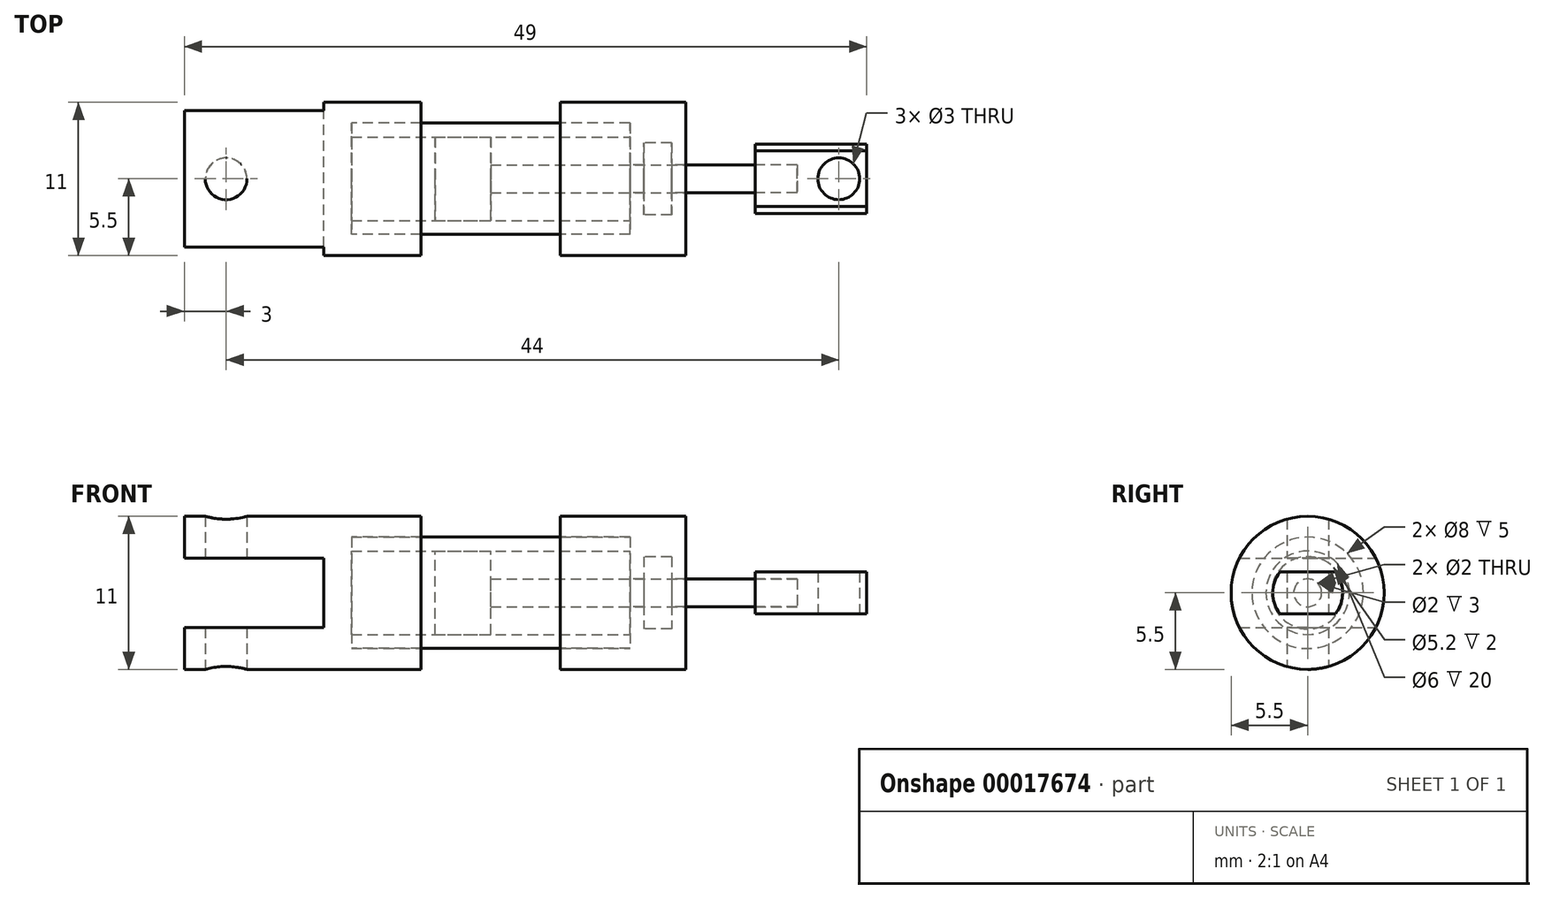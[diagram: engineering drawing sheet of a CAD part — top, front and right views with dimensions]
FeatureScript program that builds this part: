
annotation { "Feature Type Name" : "Feature", "Feature Type Description" : "" }
export const myFeature = defineFeature(function(context is Context, id is Id, definition is map)
    precondition{}
    {
        {
            var Q0;
            Q0=qCreatedBy(makeId("Front.planeOp"),FACE);
            var sketch = newSketch(context, id + "F0", { "sketchPlane" : qUnion([Q0])});
            skLineSegment(sketch, "E0", {"start": v(0, 0) * mm, "end": v(-30.47, 0) * mm, "construction": true});
            skLineSegment(sketch, "E1", {"start": v(0, 0) * mm, "end": v(0, 1) * mm});
            skLineSegment(sketch, "E2", {"start": v(0, 1) * mm, "end": v(-22, 1) * mm});
            skLineSegment(sketch, "E3", {"start": v(-22, 1) * mm, "end": v(-22, 3) * mm});
            skLineSegment(sketch, "E4", {"start": v(-22, 3) * mm, "end": v(-26, 3) * mm});
            skLineSegment(sketch, "E5", {"start": v(-26, 3) * mm, "end": v(-26, 0) * mm});
            skLineSegment(sketch, "E6", {"start": v(-26, 0) * mm, "end": v(0, 0) * mm});
            skLineSegment(sketch, "E7", {"start": v(-12, 3) * mm, "end": v(-12, 4) * mm});
            skLineSegment(sketch, "E8", {"start": v(-12, 4) * mm, "end": v(-32, 4) * mm});
            skLineSegment(sketch, "E9", {"start": v(-32, 4) * mm, "end": v(-32, 3) * mm});
            skLineSegment(sketch, "E10", {"start": v(-27, 3) * mm, "end": v(-12, 3) * mm});
            skLineSegment(sketch, "E11", {"start": v(-17, 4) * mm, "end": v(-17, 5.5) * mm});
            skLineSegment(sketch, "E12", {"start": v(-17, 5.5) * mm, "end": v(-8, 5.5) * mm});
            skLineSegment(sketch, "E13", {"start": v(-8, 5.5) * mm, "end": v(-8, 1) * mm});
            skLineSegment(sketch, "E14", {"start": v(-8, 1) * mm, "end": v(-12, 1) * mm});
            skLineSegment(sketch, "E15", {"start": v(-12, 1) * mm, "end": v(-12, 3) * mm});
            skLineSegment(sketch, "E16.bottom", {"start": v(-11, 1) * mm, "end": v(-9, 1) * mm});
            skLineSegment(sketch, "E16.top", {"start": v(-11, 2.6) * mm, "end": v(-9, 2.6) * mm});
            skLineSegment(sketch, "E16.left", {"start": v(-11, 1) * mm, "end": v(-11, 2.6) * mm});
            skLineSegment(sketch, "E16.right", {"start": v(-9, 1) * mm, "end": v(-9, 2.6) * mm});
            skLineSegment(sketch, "E17", {"start": v(-3, 1) * mm, "end": v(-3, 2.5) * mm});
            skLineSegment(sketch, "E18", {"start": v(-3, 2.5) * mm, "end": v(5, 2.5) * mm});
            skLineSegment(sketch, "E19", {"start": v(5, 2.5) * mm, "end": v(5, 0) * mm});
            skLineSegment(sketch, "E20", {"start": v(5, 0) * mm, "end": v(0, 0) * mm});
            skLineSegment(sketch, "E21", {"start": v(-27, 3) * mm, "end": v(-32, 3) * mm});
            skPoint(sketch, "E22.start.orphan", {"position": v(-32, 0) * mm});
            skLineSegment(sketch, "E23", {"start": v(-27, 4) * mm, "end": v(-27, 5.5) * mm});
            skLineSegment(sketch, "E24", {"start": v(-27, 5.5) * mm, "end": v(-44, 5.5) * mm});
            skLineSegment(sketch, "E25", {"start": v(-44, 5.5) * mm, "end": v(-44, 0) * mm});
            skLineSegment(sketch, "E26", {"start": v(-44, 0) * mm, "end": v(-32, 0) * mm});
            skLineSegment(sketch, "E27", {"start": v(-32, 3) * mm, "end": v(-32, 0) * mm});
            skSolve(sketch);
        }
        {
            var Q0;
            {var subQ7=sQuery(id+"F0.wireOp",EDGE,"E7");Q0=makeQuery(id+"F0.imprint","IMPRINT",FACE,{"disambiguationData":[TD([[makeQuery(id+"F0.imprint","IMPRINT",EDGE,{"derivedFrom":subQ7}),1.0]])]});}
            var Q1;
            Q1=sQuery(id+"F0.wireOp",EDGE,"E0");
            revolve(context, id + "F1", {"entities" : qUnion([Q0]), "axis" : qUnion([Q1]), "revolveType" : RevolveType.FULL});
        }
        {
            var Q0;
            {var subQ9=sQuery(id+"F0.wireOp",EDGE,"E1");Q0=makeQuery(id+"F0.imprint","IMPRINT",FACE,{"disambiguationData":[TD([[makeQuery(id+"F0.imprint","IMPRINT",EDGE,{"derivedFrom":subQ9}),1.0]])]});}
            var Q1;
            Q1=sQuery(id+"F0.wireOp",EDGE,"E0");
            revolve(context, id + "F2", {"entities" : qUnion([Q0]), "axis" : qUnion([Q1]), "revolveType" : RevolveType.FULL});
        }
        {
            var Q0;
            {var subQ9=sQuery(id+"F0.wireOp",EDGE,"E7");Q0=makeQuery(id+"F0.imprint","IMPRINT",FACE,{"disambiguationData":[TD([[makeQuery(id+"F0.imprint","IMPRINT",EDGE,{"derivedFrom":subQ9}),-1.0]])]});}
            var Q1;
            Q1=sQuery(id+"F0.wireOp",EDGE,"E6");
            revolve(context, id + "F3", {"entities" : qUnion([Q0]), "axis" : qUnion([Q1]), "revolveType" : RevolveType.FULL});
        }
        {
            var Q0;
            {var subQ2=sQuery(id+"F0.wireOp",EDGE,"E1");Q0=makeQuery(id+"F0.imprint","IMPRINT",FACE,{"disambiguationData":[TD([[makeQuery(id+"F0.imprint","IMPRINT",EDGE,{"derivedFrom":subQ2}),-1.0]])]});}
            var Q1;
            Q1=sQuery(id+"F0.wireOp",EDGE,"E6");
            revolve(context, id + "F4", {"entities" : qUnion([Q0]), "axis" : qUnion([Q1]), "revolveType" : RevolveType.FULL});
        }
        {
            var Q0;
            {var subQ1=sQuery(id+"F0.wireOp",EDGE,"E9");Q0=makeQuery(id+"F0.imprint","IMPRINT",FACE,{"disambiguationData":[TD([[makeQuery(id+"F0.imprint","IMPRINT",EDGE,{"derivedFrom":subQ1}),-1.0]])]});}
            var Q1;
            Q1=sQuery(id+"F0.wireOp",EDGE,"E26");
            revolve(context, id + "F5", {"entities" : qUnion([Q0]), "axis" : qUnion([Q1]), "revolveType" : RevolveType.FULL});
        }
        {
            var Q0;
            Q0=makeQuery(id+"F4.opRevolve","SWEPT_FACE",FACE,{"disambiguationData":[OSD([sQuery(id+"F0.wireOp",EDGE,"E19")])]});
            var sketch = newSketch(context, id + "F6", { "sketchPlane" : qUnion([Q0])});
            skLineSegment(sketch, "E28.bottom", {"start": v(-2, -1.5) * mm, "end": v(2, -1.5) * mm});
            skLineSegment(sketch, "E28.top", {"start": v(-2, 1.5) * mm, "end": v(2, 1.5) * mm});
            skLineSegment(sketch, "E28.left", {"start": v(-2, -1.5) * mm, "end": v(-2, 1.5) * mm});
            skLineSegment(sketch, "E28.right", {"start": v(2, -1.5) * mm, "end": v(2, 1.5) * mm});
            skSolve(sketch);
        }
        {
            var Q0;
            {var subQ1=sQuery(id+"F6.wireOp",EDGE,"E28.bottom");Q0=makeQuery(id+"F6.imprint","IMPRINT",FACE,{"disambiguationData":[TD([[makeQuery(id+"F6.imprint","IMPRINT",EDGE,{"derivedFrom":subQ1}),-1.0]])]});}
            var Q1;
            {var subQ1=sQuery(id+"F6.wireOp",EDGE,"E28.top");Q1=makeQuery(id+"F6.imprint","IMPRINT",FACE,{"disambiguationData":[TD([[makeQuery(id+"F6.imprint","IMPRINT",EDGE,{"derivedFrom":subQ1}),1.0]])]});}
            extrude(context, id + "F7", {"entities" : qUnion([Q0, Q1]), "operationType" : NewBodyOperationType.REMOVE, "oppositeDirection" : true, "depth" : 8 * mm});
        }
        {
            var Q0;
            Q0=makeQuery(id+"F7.boolean.opBoolean","COPY",FACE,{"derivedFrom":makeQuery(id+"F7.opExtrude","SWEPT_FACE",FACE,{"disambiguationData":[OSD([sQuery(id+"F6.wireOp",EDGE,"E28.bottom")])]})});
            var sketch = newSketch(context, id + "F8", { "sketchPlane" : qUnion([Q0])});
            skLineSegment(sketch, "E29", {"start": v(5, 0) * mm, "end": v(-3, 0) * mm, "construction": true});
            skCircle(sketch, "E30", {"center": v(3, 0) * mm, "radius": 1.5 * mm});
            skSolve(sketch);
        }
        {
            var Q0;
            Q0 = qSketchRegion(id + "F8", true);
            extrude(context, id + "F9", {"entities" : qUnion([Q0]), "operationType" : NewBodyOperationType.REMOVE, "oppositeDirection" : true, "depth" : 25 * mm});
        }
        {
            var Q0;
            Q0=makeQuery(id+"F5.opRevolve","SWEPT_FACE",FACE,{"disambiguationData":[OSD([sQuery(id+"F0.wireOp",EDGE,"E25")])]});
            var sketch = newSketch(context, id + "F10", { "sketchPlane" : qUnion([Q0])});
            skLineSegment(sketch, "E31.bottom", {"start": v(4.9, 2.5) * mm, "end": v(-4.9, 2.5) * mm});
            skLineSegment(sketch, "E31.top", {"start": v(4.9, -2.5) * mm, "end": v(-4.9, -2.5) * mm});
            skLineSegment(sketch, "E31.left", {"start": v(4.9, 2.5) * mm, "end": v(4.9, -2.5) * mm});
            skLineSegment(sketch, "E31.right", {"start": v(-4.9, 2.5) * mm, "end": v(-4.9, -2.5) * mm});
            skSolve(sketch);
        }
        {
            var Q0;
            Q0 = qSketchRegion(id + "F10", true);
            var Q1;
            {var subQ1=sQuery(id+"F10.wireOp",EDGE,"E31.left");Q1=makeQuery(id+"F10.imprint","IMPRINT",FACE,{"disambiguationData":[TD([[makeQuery(id+"F10.imprint","IMPRINT",EDGE,{"derivedFrom":subQ1}),1.0]])]});}
            var Q2;
            {var subQ1=sQuery(id+"F10.wireOp",EDGE,"E31.right");Q2=makeQuery(id+"F10.imprint","IMPRINT",FACE,{"disambiguationData":[TD([[makeQuery(id+"F10.imprint","IMPRINT",EDGE,{"derivedFrom":subQ1}),-1.0]])]});}
            extrude(context, id + "F11", {"entities" : qUnion([Q0, Q1, Q2]), "operationType" : NewBodyOperationType.REMOVE, "oppositeDirection" : true, "depth" : 10 * mm});
        }
        {
            var Q0;
            Q0=makeQuery(id+"F11.boolean.opBoolean","COPY",FACE,{"derivedFrom":makeQuery(id+"F11.opExtrude","SWEPT_FACE",FACE,{"disambiguationData":[OSD([sQuery(id+"F10.wireOp",EDGE,"E31.bottom")])]})});
            var sketch = newSketch(context, id + "F12", { "sketchPlane" : qUnion([Q0])});
            skLineSegment(sketch, "E32", {"start": v(-44, 0) * mm, "end": v(-31.6, 0) * mm, "construction": true});
            skCircle(sketch, "E33", {"center": v(-41, 0) * mm, "radius": 1.5 * mm});
            skSolve(sketch);
        }
        {
            var Q0;
            Q0=makeQuery(id+"F12.imprint","IMPRINT",FACE,{"disambiguationData":[TD([[makeQuery(id+"F12.imprint","IMPRINT",EDGE,{"derivedFrom":sQuery(id+"F12.wireOp",EDGE,"E33")}),1.0]])]});
            extrude(context, id + "F13", {"entities" : qUnion([Q0]), "operationType" : NewBodyOperationType.REMOVE, "oppositeDirection" : true, "depth" : 25 * mm, "hasSecondDirection" : true, "secondDirectionOppositeDirection" : false, "secondDirectionDepth" : 25 * mm});
        }
    });
